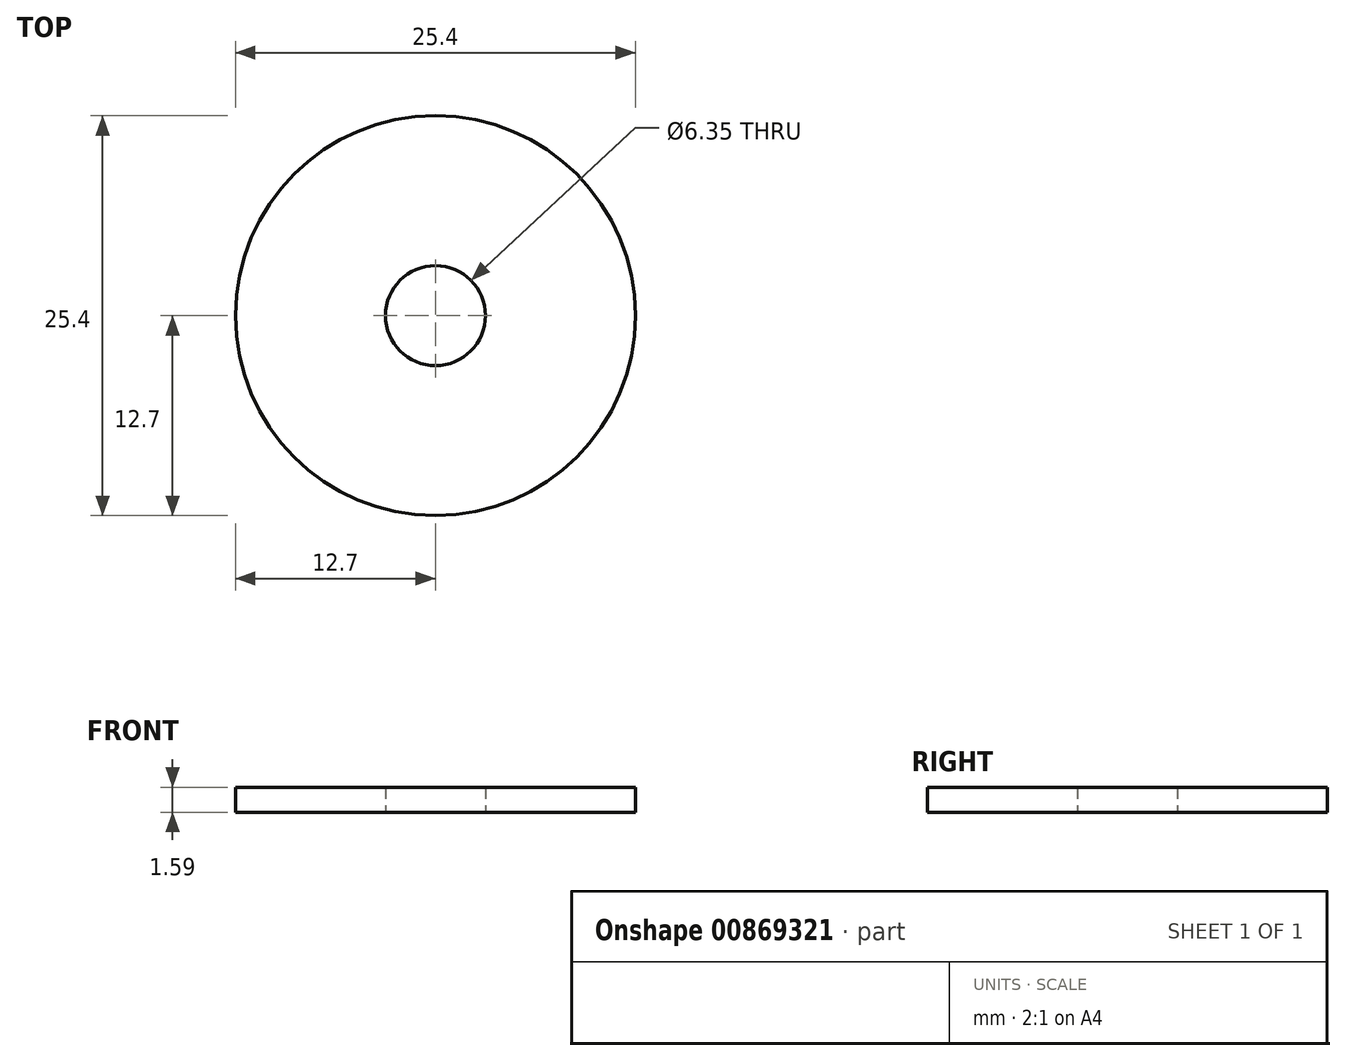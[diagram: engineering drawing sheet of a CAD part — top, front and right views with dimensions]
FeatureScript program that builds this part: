
annotation { "Feature Type Name" : "Feature", "Feature Type Description" : "" }
export const myFeature = defineFeature(function(context is Context, id is Id, definition is map)
    precondition{}
    {
        {
            var Q0;
            Q0=qCreatedBy(makeId("Top.planeOp"),FACE);
            var sketch = newSketch(context, id + "F0", { "sketchPlane" : qUnion([Q0])});
            skCircle(sketch, "E0", {"center": v(0, 0) * mm, "radius": 3.18 * mm});
            skCircle(sketch, "E1", {"center": v(0, 0) * mm, "radius": 12.7 * mm});
            skSolve(sketch);
        }
        {
            var Q0;
            Q0 = qSketchRegion(id + "F0", true);
            extrude(context, id + "F1", {"entities" : qUnion([Q0]), "depth" : 1.59 * mm, "offsetDistance" : 25.4 * mm});
        }
    });
